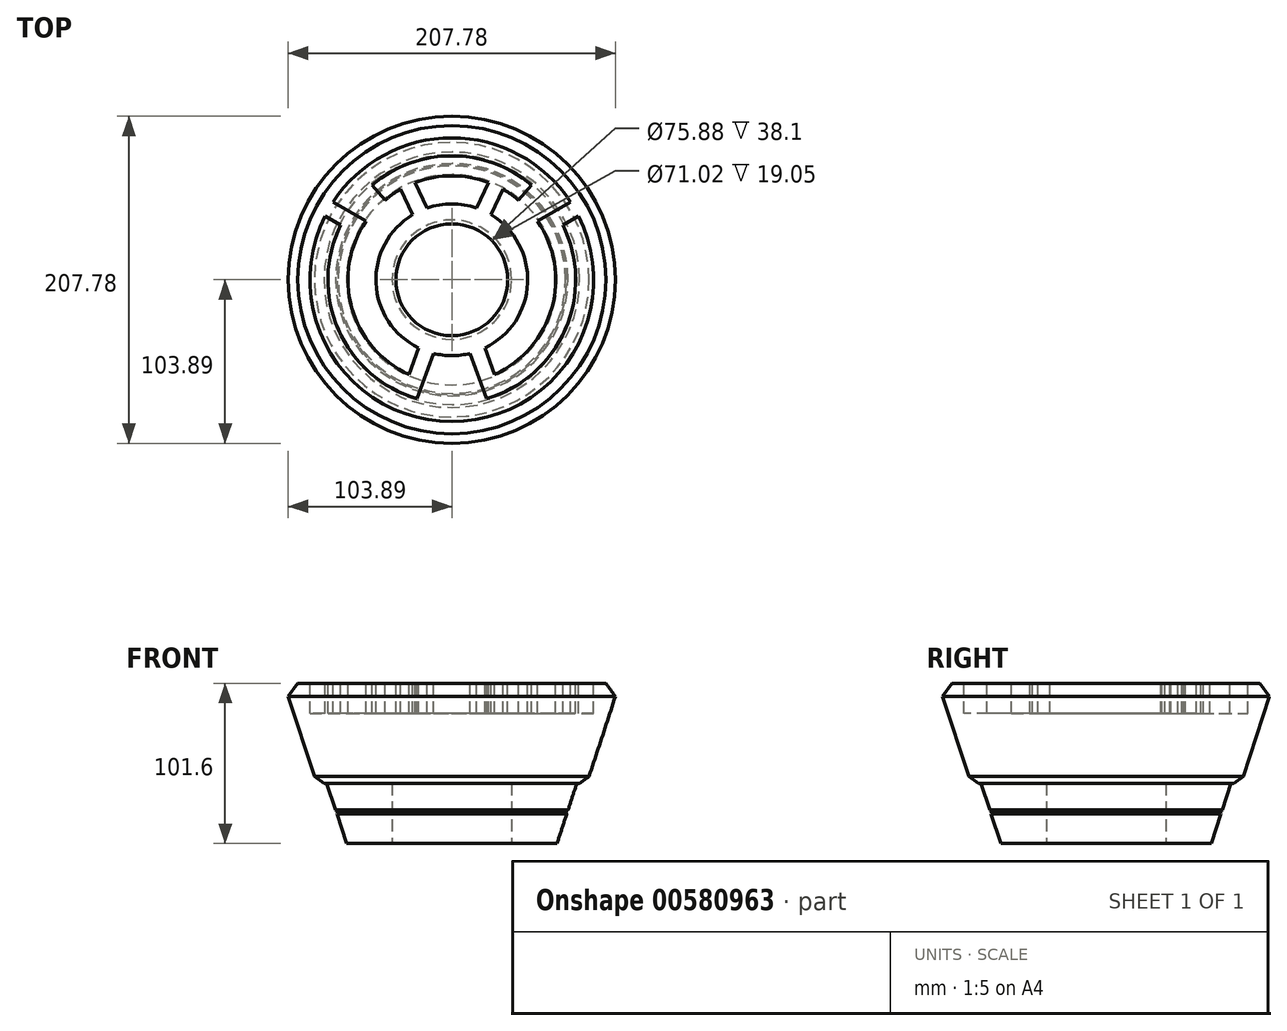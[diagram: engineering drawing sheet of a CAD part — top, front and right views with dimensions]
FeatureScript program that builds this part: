
annotation { "Feature Type Name" : "Feature", "Feature Type Description" : "" }
export const myFeature = defineFeature(function(context is Context, id is Id, definition is map)
    precondition{}
    {
        {
            var Q0;
            Q0=qCreatedBy(makeId("Top.planeOp"),FACE);
            var sketch = newSketch(context, id + "F0", { "sketchPlane" : qUnion([Q0])});
            skCircle(sketch, "E0", {"center": v(0, 0) * mm, "radius": 66.85 * mm});
            skSolve(sketch);
        }
        {
            var Q0;
            Q0=qCreatedBy(makeId("Top.planeOp"),FACE);
            cPlane(context, id + "F1", {"entities" : qUnion([Q0]), "cplaneType" : CPlaneType.OFFSET, "offset" : 101.6 * mm, "width" : 152.4 * mm, "height" : 152.4 * mm});
        }
        {
            var Q0;
            Q0=qCreatedBy(id+"F1.planeOp",FACE);
            var sketch = newSketch(context, id + "F2", { "sketchPlane" : qUnion([Q0])});
            skCircle(sketch, "E1", {"center": v(0, 0) * mm, "radius": 100.28 * mm});
            skSolve(sketch);
        }
        {
            var Q0;
            Q0=makeQuery(id+"F2.imprint","IMPRINT",FACE,{"disambiguationData":[TD([[makeQuery(id+"F2.imprint","IMPRINT",EDGE,{"derivedFrom":sQuery(id+"F2.wireOp",EDGE,"E1")}),1.0]])]});
            var Q1;
            Q1=makeQuery(id+"F0.imprint","IMPRINT",FACE,{"disambiguationData":[TD([[makeQuery(id+"F0.imprint","IMPRINT",EDGE,{"derivedFrom":sQuery(id+"F0.wireOp",EDGE,"E0")}),1.0]])]});
            var Q2;
            Q2=sQuery(id+"F2.wireOp",EDGE,"Eyu8YDiN-lEGU-Wuxt-0ncA-RZLAWeJK4OgB");
            var Q3;
            Q3=sQuery(id+"F0.wireOp",EDGE,"fgfE4CqQ-t5n6-ucAx-yhIW-5wF2yx0Jya2k");
            loft(context, id + "F3", {"sheetProfilesArray" : [{ "sheetProfileEntities" : qUnion([Q0]) }, { "sheetProfileEntities" : qUnion([Q1]) }], "wireProfilesArray" : [{ "wireProfileEntities" : qUnion([Q2]) }, { "wireProfileEntities" : qUnion([Q3]) }]});
        }
        {
            var Q0;
            Q0=qCreatedBy(makeId("Top.planeOp"),FACE);
            var sketch = newSketch(context, id + "F4", { "sketchPlane" : qUnion([Q0])});
            skCircle(sketch, "E2", {"center": v(0, 0) * mm, "radius": 37.94 * mm});
            skSolve(sketch);
        }
        {
            var Q0;
            Q0=makeQuery(id+"F4.imprint","IMPRINT",FACE,{"disambiguationData":[TD([[makeQuery(id+"F4.imprint","IMPRINT",EDGE,{"derivedFrom":sQuery(id+"F4.wireOp",EDGE,"E2")}),1.0]])]});
            extrude(context, id + "F5", {"entities" : qUnion([Q0]), "operationType" : NewBodyOperationType.REMOVE, "depth" : 53.34 * mm, "offsetDistance" : 25.4 * mm});
        }
        {
            var Q0;
            Q0=qCreatedBy(makeId("Top.planeOp"),FACE);
            cPlane(context, id + "F6", {"entities" : qUnion([Q0]), "cplaneType" : CPlaneType.OFFSET, "offset" : 38.1 * mm, "width" : 152.4 * mm, "height" : 152.4 * mm});
        }
        {
            var Q0;
            Q0=qCreatedBy(id+"F6.planeOp",FACE);
            var sketch = newSketch(context, id + "F7", { "sketchPlane" : qUnion([Q0])});
            skCircle(sketch, "E3", {"center": v(0, 0) * mm, "radius": 85.73 * mm});
            skSolve(sketch);
        }
        {
            var Q0;
            Q0=qCreatedBy(id+"F1.planeOp",FACE);
            var sketch = newSketch(context, id + "F8", { "sketchPlane" : qUnion([Q0])});
            skCircle(sketch, "E4", {"center": v(0, 0) * mm, "radius": 106.63 * mm});
            skSolve(sketch);
        }
        {
            var Q1;
            Q1=makeQuery(id+"F7.imprint","IMPRINT",FACE,{"disambiguationData":[TD([[makeQuery(id+"F7.imprint","IMPRINT",EDGE,{"derivedFrom":sQuery(id+"F7.wireOp",EDGE,"E3")}),1.0]])]});
            var Q2;
            Q2=makeQuery(id+"F8.imprint","IMPRINT",FACE,{"disambiguationData":[TD([[makeQuery(id+"F8.imprint","IMPRINT",EDGE,{"derivedFrom":sQuery(id+"F8.wireOp",EDGE,"E4")}),1.0]])]});
            loft(context, id + "F9", {"operationType" : NewBodyOperationType.ADD, "sheetProfilesArray" : [{ "sheetProfileEntities" : qUnion([Q1]) }, { "sheetProfileEntities" : qUnion([Q2]) }]});
        }
        {
            var Q0;
            Q0=makeQuery(id+"F9.opLoft","MID_CAP_EDGE",EDGE,{"disambiguationData":[OSD([sQuery(id+"F7.wireOp",EDGE,"E3")])],"capPos":0.0});
            chamfer(context, id + "F10", {"entities" : qUnion([Q0]), "width" : 6.35 * mm, "tangentPropagation" : true});
        }
        {
            var Q0;
            Q0=makeQuery(id+"F9.opLoft","MID_CAP_EDGE",EDGE,{"disambiguationData":[OSD([sQuery(id+"F7.wireOp",EDGE,"E3"),sQuery(id+"F8.wireOp",EDGE,"E4")])],"capPos":1.0});
            chamfer(context, id + "F11", {"entities" : qUnion([Q0]), "width" : 6.35 * mm, "tangentPropagation" : true});
        }
        {
            var Q0;
            Q0=qCreatedBy(makeId("Front.planeOp"),FACE);
            var sketch = newSketch(context, id + "F12", { "sketchPlane" : qUnion([Q0])});
            skLineSegment(sketch, "E5", {"start": v(-79.4, 38.11) * mm, "end": v(-66.85, 0) * mm});
            skLineSegment(sketch, "E6", {"start": v(-73.8, 21.14) * mm, "end": v(-72.2, 20.33) * mm});
            skLineSegment(sketch, "E7", {"start": v(-72.2, 20.33) * mm, "end": v(-73.02, 18.73) * mm});
            skSolve(sketch);
        }
        {
            var Q0;
            Q0=qCreatedBy(makeId("Right.planeOp"),FACE);
            var sketch = newSketch(context, id + "F13", { "sketchPlane" : qUnion([Q0])});
            skLineSegment(sketch, "E8", {"start": v(0, 0) * mm, "end": v(0, 184.2) * mm});
            skSolve(sketch);
        }
        {
            var Q0;
            Q0=qSketchRegion(id+"F12",true);
            var Q1;
            Q1=sQuery(id+"F13.wireOp",EDGE,"E8");
            revolve(context, id + "F14", {"operationType" : NewBodyOperationType.REMOVE, "entities" : qUnion([Q0]), "axis" : qUnion([Q1]), "revolveType" : RevolveType.FULL, "oppositeDirection" : true});
        }
        {
            var Q0;
            Q0=makeQuery(id+"F9.boolean.opBoolean","MERGE",FACE,{"derivedFrom":[makeQuery(id+"F3.opLoft","CAP_FACE",FACE,{"disambiguationData":[OSD([makeQuery(id+"F2.imprint","IMPRINT",FACE,{"disambiguationData":[TD([[makeQuery(id+"F2.imprint","IMPRINT",EDGE,{"derivedFrom":sQuery(id+"F2.wireOp",EDGE,"E1")}),1.0]])]})])],"isStart":true}),makeQuery(id+"F9.opLoft","CAP_FACE",FACE,{"disambiguationData":[OSD([makeQuery(id+"F8.imprint","IMPRINT",FACE,{"disambiguationData":[TD([[makeQuery(id+"F8.imprint","IMPRINT",EDGE,{"derivedFrom":sQuery(id+"F8.wireOp",EDGE,"E4")}),1.0]])]})])],"isStart":true})]});
            var sketch = newSketch(context, id + "F15", { "sketchPlane" : qUnion([Q0])});
            skCircle(sketch, "E9", {"center": v(0, 0) * mm, "radius": 100.28 * mm});
            skCircle(sketch, "E10.0", {"center": v(0, 0) * mm, "radius": 35.5 * mm});
            skLineSegment(sketch, "E11", {"start": v(0, 0) * mm, "end": v(0, 10.8) * mm});
            skLineSegment(sketch, "E12", {"start": v(0, 0) * mm, "end": v(13.67, 0) * mm});
            skArc(sketch, "E13", {"start": v(-70.55, 34.86) * mm, "mid": v(0, -78.69) * mm, "end": v(70.55, 34.86) * mm});
            skArc(sketch, "E14", {"start": v(-17.73, -63.56) * mm, "mid": v(0, -65.99) * mm, "end": v(17.73, -63.56) * mm});
            skArc(sketch, "E15", {"start": v(-11.62, -46.79) * mm, "mid": v(0, -48.2) * mm, "end": v(11.62, -46.79) * mm});
            skLineSegment(sketch, "E16", {"start": v(-4.62, 2.15) * mm, "end": v(-16.8, -31.29) * mm});
            skLineSegment(sketch, "E17", {"start": v(4.45, -2.64) * mm, "end": v(-22.08, -75.53) * mm});
            skArc(sketch, "E18", {"start": v(-80.46, 40.59) * mm, "mid": v(0, -90.12) * mm, "end": v(80.46, 40.59) * mm});
            skLineSegment(sketch, "E19", {"start": v(2.54, 4.4) * mm, "end": v(-27.9, 21.97) * mm});
            skLineSegment(sketch, "E20", {"start": v(-4.38, -3.34) * mm, "end": v(-32.98, 13.17) * mm});
            skLineSegment(sketch, "E21.trimOffspring", {"start": v(-70.55, 34.86) * mm, "end": v(-80.46, 40.59) * mm});
            skPoint(sketch, "E22.orphan", {"position": v(-31.63, -72.05) * mm});
            skLineSegment(sketch, "E23.trimOffspring", {"start": v(-21.17, -43.31) * mm, "end": v(-27.28, -60.09) * mm});
            skLineSegment(sketch, "E24.trimOffspring", {"start": v(-54.44, 37.3) * mm, "end": v(-75.38, 49.39) * mm});
            skLineSegment(sketch, "E25.MirrorCS", {"start": v(70.55, 34.86) * mm, "end": v(80.46, 40.59) * mm});
            skLineSegment(sketch, "E26.MirrorCS", {"start": v(54.44, 37.3) * mm, "end": v(75.38, 49.39) * mm});
            skLineSegment(sketch, "E27.MirrorCS", {"start": v(21.17, -43.31) * mm, "end": v(27.28, -60.09) * mm});
            skLineSegment(sketch, "E28.MirrorCS", {"start": v(-4.45, -2.64) * mm, "end": v(22.08, -75.53) * mm});
            skArc(sketch, "E29.trimOffspring", {"start": v(65.47, 43.66) * mm, "mid": v(0, 78.69) * mm, "end": v(-65.47, 43.66) * mm});
            skArc(sketch, "E30.trimOffspring", {"start": v(75.38, 49.39) * mm, "mid": v(0, 90.12) * mm, "end": v(-75.38, 49.39) * mm});
            skArc(sketch, "E31.trimOffspring", {"start": v(27.28, -60.09) * mm, "mid": v(65.93, -2.88) * mm, "end": v(32.4, 57.48) * mm});
            skArc(sketch, "E32.trimOffspring", {"start": v(21.17, -43.31) * mm, "mid": v(48.16, -2.1) * mm, "end": v(24.86, 41.3) * mm});
            skLineSegment(sketch, "E33", {"start": v(0, 0) * mm, "end": v(-22.83, 27.2) * mm});
            skLineSegment(sketch, "E34", {"start": v(-4.38, -2.64) * mm, "end": v(-19.46, 29.7) * mm});
            skLineSegment(sketch, "E35", {"start": v(4.74, 1.84) * mm, "end": v(-10.25, 34) * mm});
            skLineSegment(sketch, "E36.trimOffspring", {"start": v(-24.86, 41.3) * mm, "end": v(-32.4, 57.48) * mm});
            skLineSegment(sketch, "E37.trimOffspring", {"start": v(-42.42, 50.55) * mm, "end": v(-50.58, 60.28) * mm});
            skArc(sketch, "E38.trimOffspring", {"start": v(-32.4, 57.48) * mm, "mid": v(-65.93, -2.88) * mm, "end": v(-27.28, -60.09) * mm});
            skArc(sketch, "E39.trimOffspring", {"start": v(-24.86, 41.3) * mm, "mid": v(-48.16, -2.1) * mm, "end": v(-21.17, -43.31) * mm});
            skLineSegment(sketch, "E40.MirrorCS", {"start": v(24.86, 41.3) * mm, "end": v(32.4, 57.48) * mm});
            skLineSegment(sketch, "E41.MirrorCS", {"start": v(42.42, 50.55) * mm, "end": v(50.58, 60.28) * mm});
            skLineSegment(sketch, "E42.MirrorCS", {"start": v(-4.74, 1.84) * mm, "end": v(10.25, 34) * mm});
            skArc(sketch, "E43.trimOffspring", {"start": v(15.66, 45.6) * mm, "mid": v(0, 48.2) * mm, "end": v(-15.66, 45.6) * mm});
            skArc(sketch, "E44.trimOffspring", {"start": v(23.2, 61.78) * mm, "mid": v(0, 65.99) * mm, "end": v(-23.2, 61.78) * mm});
            skLineSegment(sketch, "E45.trimOffspring", {"start": v(15.66, 45.6) * mm, "end": v(23.2, 61.78) * mm});
            skLineSegment(sketch, "E46.trimOffspring", {"start": v(-15.66, 45.6) * mm, "end": v(-23.2, 61.78) * mm});
            skPoint(sketch, "E47.orphan", {"position": v(-28.58, 73.32) * mm});
            skPoint(sketch, "E48.orphan", {"position": v(28.58, 73.32) * mm});
            skSolve(sketch);
        }
        {
            var Q0;
            {var subQ0=sQuery(id+"F15.wireOp",EDGE,"E14");Q0=makeQuery(id+"F15.imprint","IMPRINT",FACE,{"disambiguationData":[TD([[makeQuery(id+"F15.imprint","IMPRINT",EDGE,{"derivedFrom":subQ0}),1.0]])]});}
            var Q1;
            {var subQ5=sQuery(id+"F15.wireOp",EDGE,"E14");Q1=makeQuery(id+"F15.imprint","IMPRINT",FACE,{"disambiguationData":[TD([[makeQuery(id+"F15.imprint","IMPRINT",EDGE,{"derivedFrom":subQ5}),-1.0]])]});}
            var Q2;
            {var subQ4=sQuery(id+"F15.wireOp",EDGE,"E23.trimOffspring");Q2=makeQuery(id+"F15.imprint","IMPRINT",FACE,{"disambiguationData":[TD([[makeQuery(id+"F15.imprint","IMPRINT",EDGE,{"derivedFrom":subQ4}),-1.0]])]});}
            var Q3;
            Q3=makeQuery(id+"F15.imprint","IMPRINT",FACE,{"disambiguationData":[TD([[makeQuery(id+"F15.imprint","IMPRINT",EDGE,{"derivedFrom":sQuery(id+"F15.wireOp",EDGE,"E18")}),1.0]])]});
            var Q4;
            {var subQ1=sQuery(id+"F15.wireOp",EDGE,"E10.0");var subQ8=makeQuery(id+"F15.imprint","IMPRINT",VERTEX,{"derivedFrom":subQ1});Q4=makeQuery(id+"F15.imprint","IMPRINT",FACE,{"disambiguationData":[TD([[makeQuery(id+"F15.imprint","IMPRINT",EDGE,{"disambiguationData":[TD([[subQ8,-1.0]])],"derivedFrom":subQ1}),1.0]])]});}
            var Q5;
            {var subQ0=sQuery(id+"F15.wireOp",EDGE,"E16");var subQ1=sQuery(id+"F15.wireOp",EDGE,"E10.0");var subQ2=makeQuery(id+"F15.imprint","INTERSECT",VERTEX,{"derivedFrom":[subQ1,subQ0]});Q5=makeQuery(id+"F15.imprint","IMPRINT",FACE,{"disambiguationData":[TD([[makeQuery(id+"F15.imprint","IMPRINT",EDGE,{"disambiguationData":[TD([[subQ2,1.0]])],"derivedFrom":subQ1}),1.0]])]});}
            var Q6;
            {var subQ3=sQuery(id+"F15.wireOp",EDGE,"E16");var subQ7=sQuery(id+"F15.wireOp",EDGE,"E10.0");var subQ9=makeQuery(id+"F15.imprint","INTERSECT",VERTEX,{"derivedFrom":[subQ7,subQ3]});Q6=makeQuery(id+"F15.imprint","IMPRINT",FACE,{"disambiguationData":[TD([[makeQuery(id+"F15.imprint","IMPRINT",EDGE,{"disambiguationData":[TD([[subQ9,-1.0]])],"derivedFrom":subQ7}),1.0]])]});}
            var Q7;
            {var subQ0=sQuery(id+"F15.wireOp",EDGE,"E17");var subQ1=sQuery(id+"F15.wireOp",EDGE,"E10.0");var subQ2=makeQuery(id+"F15.imprint","INTERSECT",VERTEX,{"derivedFrom":[subQ1,subQ0]});Q7=makeQuery(id+"F15.imprint","IMPRINT",FACE,{"disambiguationData":[TD([[makeQuery(id+"F15.imprint","IMPRINT",EDGE,{"disambiguationData":[TD([[subQ2,-1.0]])],"derivedFrom":subQ1}),1.0]])]});}
            var Q8;
            {var subQ1=sQuery(id+"F15.wireOp",EDGE,"E10.0");var subQ7=sQuery(id+"F15.wireOp",EDGE,"E19");var subQ8=makeQuery(id+"F15.imprint","INTERSECT",VERTEX,{"derivedFrom":[subQ1,subQ7]});Q8=makeQuery(id+"F15.imprint","IMPRINT",FACE,{"disambiguationData":[TD([[makeQuery(id+"F15.imprint","IMPRINT",EDGE,{"disambiguationData":[TD([[subQ8,-1.0]])],"derivedFrom":subQ1}),1.0]])]});}
            var Q9;
            {var subQ0=sQuery(id+"F15.wireOp",EDGE,"E19");var subQ1=sQuery(id+"F15.wireOp",EDGE,"E10.0");var subQ2=makeQuery(id+"F15.imprint","INTERSECT",VERTEX,{"derivedFrom":[subQ1,subQ0]});Q9=makeQuery(id+"F15.imprint","IMPRINT",FACE,{"disambiguationData":[TD([[makeQuery(id+"F15.imprint","IMPRINT",EDGE,{"disambiguationData":[TD([[subQ2,1.0]])],"derivedFrom":subQ1}),1.0]])]});}
            var Q10;
            {var subQ1=sQuery(id+"F15.wireOp",EDGE,"E16");var subQ7=sQuery(id+"F15.wireOp",EDGE,"E42.MirrorCS");var subQ9=makeQuery(id+"F15.imprint","INTERSECT",VERTEX,{"derivedFrom":[subQ1,subQ7]});Q10=makeQuery(id+"F15.imprint","IMPRINT",FACE,{"disambiguationData":[TD([[makeQuery(id+"F15.imprint","IMPRINT",EDGE,{"disambiguationData":[TD([[subQ9,-1.0]])],"derivedFrom":subQ1}),-1.0]])]});}
            var Q11;
            {var subQ0=sQuery(id+"F15.wireOp",EDGE,"E42.MirrorCS");var subQ1=sQuery(id+"F15.wireOp",EDGE,"E19");var subQ2=makeQuery(id+"F15.imprint","INTERSECT",VERTEX,{"derivedFrom":[subQ1,subQ0]});Q11=makeQuery(id+"F15.imprint","IMPRINT",FACE,{"disambiguationData":[TD([[makeQuery(id+"F15.imprint","IMPRINT",EDGE,{"disambiguationData":[TD([[subQ2,-1.0]])],"derivedFrom":subQ1}),1.0]])]});}
            var Q12;
            {var subQ3=sQuery(id+"F15.wireOp",EDGE,"E34");var subQ5=sQuery(id+"F15.wireOp",EDGE,"E10.0");var subQ6=makeQuery(id+"F15.imprint","INTERSECT",VERTEX,{"derivedFrom":[subQ5,subQ3]});Q12=makeQuery(id+"F15.imprint","IMPRINT",FACE,{"disambiguationData":[TD([[makeQuery(id+"F15.imprint","IMPRINT",EDGE,{"disambiguationData":[TD([[subQ6,1.0]])],"derivedFrom":subQ5}),1.0]])]});}
            var Q13;
            {var subQ0=sQuery(id+"F15.wireOp",EDGE,"E33");var subQ1=sQuery(id+"F15.wireOp",EDGE,"E10.0");var subQ2=makeQuery(id+"F15.imprint","INTERSECT",VERTEX,{"derivedFrom":[subQ1,subQ0]});Q13=makeQuery(id+"F15.imprint","IMPRINT",FACE,{"disambiguationData":[TD([[makeQuery(id+"F15.imprint","IMPRINT",EDGE,{"disambiguationData":[TD([[subQ2,1.0]])],"derivedFrom":subQ1}),1.0]])]});}
            var Q14;
            {var subQ0=sQuery(id+"F15.wireOp",EDGE,"E35");var subQ1=sQuery(id+"F15.wireOp",EDGE,"E10.0");var subQ2=makeQuery(id+"F15.imprint","INTERSECT",VERTEX,{"derivedFrom":[subQ1,subQ0]});Q14=makeQuery(id+"F15.imprint","IMPRINT",FACE,{"disambiguationData":[TD([[makeQuery(id+"F15.imprint","IMPRINT",EDGE,{"disambiguationData":[TD([[subQ2,1.0]])],"derivedFrom":subQ1}),1.0]])]});}
            var Q15;
            {var subQ0=sQuery(id+"F15.wireOp",EDGE,"E33");var subQ1=sQuery(id+"F15.wireOp",EDGE,"E11");var subQ2=makeQuery(id+"F15.imprint","INTERSECT",VERTEX,{"derivedFrom":[subQ1,subQ0]});Q15=makeQuery(id+"F15.imprint","IMPRINT",FACE,{"disambiguationData":[TD([[makeQuery(id+"F15.imprint","IMPRINT",EDGE,{"disambiguationData":[TD([[subQ2,-1.0]])],"derivedFrom":subQ1}),1.0]])]});}
            var Q16;
            Q16=makeQuery(id+"F15.imprint","IMPRINT",FACE,{"disambiguationData":[TD([[makeQuery(id+"F15.imprint","IMPRINT",EDGE,{"derivedFrom":sQuery(id+"F15.wireOp",EDGE,"E43.trimOffspring")}),-1.0]])]});
            var Q17;
            {var subQ4=sQuery(id+"F15.wireOp",EDGE,"E30.trimOffspring");Q17=makeQuery(id+"F15.imprint","IMPRINT",FACE,{"disambiguationData":[TD([[makeQuery(id+"F15.imprint","IMPRINT",EDGE,{"derivedFrom":subQ4}),1.0]])]});}
            var Q18;
            {var subQ5=sQuery(id+"F15.wireOp",EDGE,"E41.MirrorCS");Q18=makeQuery(id+"F15.imprint","IMPRINT",FACE,{"disambiguationData":[TD([[makeQuery(id+"F15.imprint","IMPRINT",EDGE,{"derivedFrom":subQ5}),-1.0]])]});}
            var Q19;
            {var subQ5=sQuery(id+"F15.wireOp",EDGE,"E37.trimOffspring");Q19=makeQuery(id+"F15.imprint","IMPRINT",FACE,{"disambiguationData":[TD([[makeQuery(id+"F15.imprint","IMPRINT",EDGE,{"derivedFrom":subQ5}),1.0]])]});}
            var Q20;
            {var subQ3=sQuery(id+"F15.wireOp",EDGE,"E27.MirrorCS");Q20=makeQuery(id+"F15.imprint","IMPRINT",FACE,{"disambiguationData":[TD([[makeQuery(id+"F15.imprint","IMPRINT",EDGE,{"derivedFrom":subQ3}),1.0]])]});}
            var Q21;
            {var subQ0=sQuery(id+"F15.wireOp",EDGE,"E33");var subQ1=sQuery(id+"F15.wireOp",EDGE,"E19");var subQ2=makeQuery(id+"F15.imprint","INTERSECT",VERTEX,{"derivedFrom":[subQ1,subQ0]});Q21=makeQuery(id+"F15.imprint","IMPRINT",FACE,{"disambiguationData":[TD([[makeQuery(id+"F15.imprint","IMPRINT",EDGE,{"disambiguationData":[TD([[subQ2,-1.0]])],"derivedFrom":subQ1}),-1.0]])]});}
            extrude(context, id + "F16", {"entities" : qUnion([Q0, Q1, Q2, Q3, Q4, Q5, Q6, Q7, Q8, Q9, Q10, Q11, Q12, Q13, Q14, Q15, Q16, Q17, Q18, Q19, Q20, Q21]), "operationType" : NewBodyOperationType.REMOVE, "oppositeDirection" : true, "depth" : 19.05 * mm, "offsetDistance" : 25.4 * mm});
        }
    });
